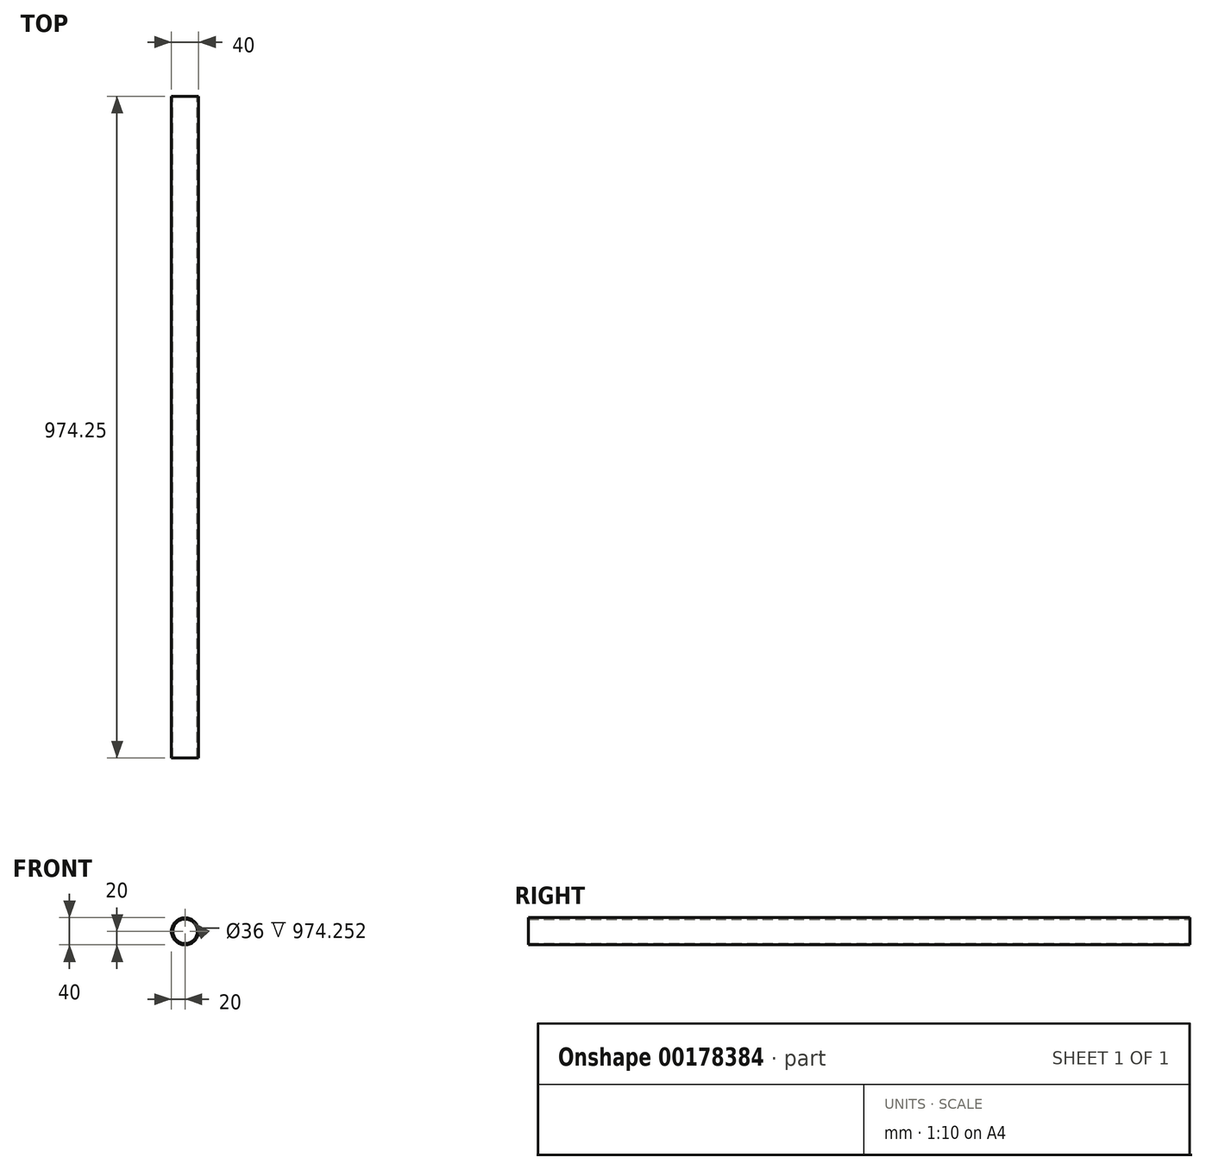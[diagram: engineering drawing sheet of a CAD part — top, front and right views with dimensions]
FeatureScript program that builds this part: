
annotation { "Feature Type Name" : "Feature", "Feature Type Description" : "" }
export const myFeature = defineFeature(function(context is Context, id is Id, definition is map)
    precondition{}
    {
        {
            var Q0;
            Q0=qCreatedBy(makeId("Front.planeOp"),FACE);
            var sketch = newSketch(context, id + "F0", { "sketchPlane" : qUnion([Q0])});
            skCircle(sketch, "E0", {"center": v(0, 0) * mm, "radius": 20 * mm});
            skCircle(sketch, "E1.0", {"center": v(0, 0) * mm, "radius": 18 * mm});
            skSolve(sketch);
        }
        {
            var Q0;
            Q0=makeQuery(id+"F0.imprint","IMPRINT",FACE,{"disambiguationData":[TD([[makeQuery(id+"F0.imprint","IMPRINT",EDGE,{"derivedFrom":sQuery(id+"F0.wireOp",EDGE,"E0")}),1.0]])]});
            extrude(context, id + "F1", {"entities" : qUnion([Q0]), "depth" : 974.25 * mm});
        }
    });
